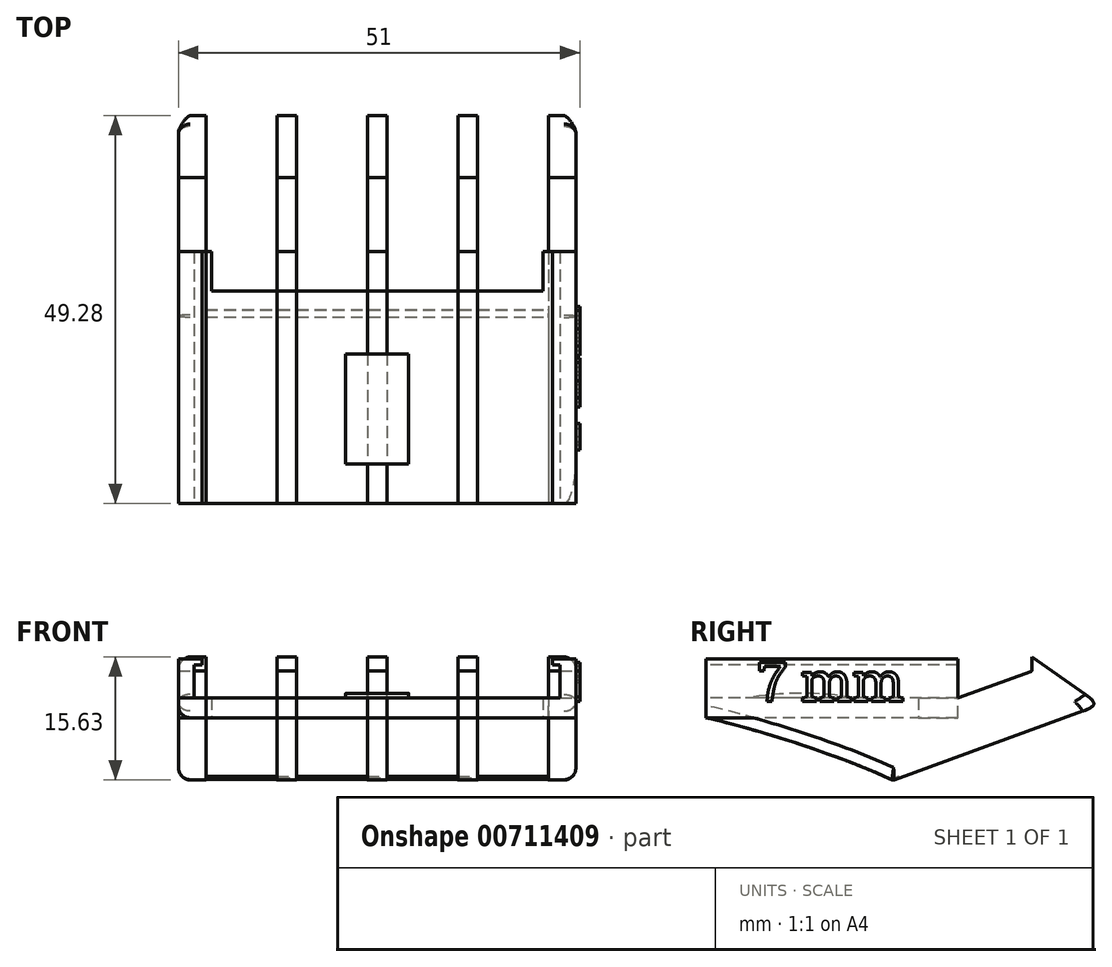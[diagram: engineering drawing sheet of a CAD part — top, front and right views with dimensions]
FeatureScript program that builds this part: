
annotation { "Feature Type Name" : "Feature", "Feature Type Description" : "" }
export const myFeature = defineFeature(function(context is Context, id is Id, definition is map)
    precondition{}
    {
        {
            var Q0;
            Q0=qCreatedBy(makeId("Top.planeOp"),FACE);
            var sketch = newSketch(context, id + "F0", { "sketchPlane" : qUnion([Q0])});
            skLineSegment(sketch, "E0.top", {"start": v(25.25, -16) * mm, "end": v(-25.25, -16) * mm});
            skLineSegment(sketch, "E0.left", {"start": v(25.25, 16) * mm, "end": v(25.25, -16) * mm});
            skLineSegment(sketch, "E0.right", {"start": v(-25.25, 16) * mm, "end": v(-25.25, -16) * mm});
            skPoint(sketch, "E0.middle", {"position": v(0, 0) * mm});
            skLineSegment(sketch, "E1", {"start": v(-21.05, 11) * mm, "end": v(21.05, 11) * mm});
            skLineSegment(sketch, "E2", {"start": v(21.05, 11) * mm, "end": v(21.05, 16) * mm});
            skLineSegment(sketch, "E3", {"start": v(21.05, 16) * mm, "end": v(25.25, 16) * mm});
            skLineSegment(sketch, "E4", {"start": v(-21.05, 11) * mm, "end": v(-21.05, 16) * mm});
            skLineSegment(sketch, "E5", {"start": v(-21.05, 16) * mm, "end": v(-25.25, 16) * mm});
            skSolve(sketch);
        }
        {
            var Q0;
            Q0 = qSketchRegion(id + "F0", true);
            extrude(context, id + "F1", {"entities" : qUnion([Q0]), "depth" : 2.5 * mm, "offsetDistance" : 25 * mm});
        }
        {
            var Q0;
            Q0=makeQuery(id+"F1.opExtrude","SWEPT_FACE",FACE,{"disambiguationData":[OSD([sQuery(id+"F0.wireOp",EDGE,"E0.top")])]});
            var sketch = newSketch(context, id + "F2", { "sketchPlane" : qUnion([Q0])});
            skLineSegment(sketch, "E6.0", {"start": v(25.25, 2.5) * mm, "end": v(-25.25, 2.5) * mm});
            skLineSegment(sketch, "E7", {"start": v(25.25, 2.5) * mm, "end": v(25.25, 7.5) * mm});
            skLineSegment(sketch, "E8", {"start": v(25.25, 7.5) * mm, "end": v(22.25, 7.5) * mm});
            skLineSegment(sketch, "E9", {"start": v(22.25, 7.5) * mm, "end": v(22.25, 6.7) * mm});
            skLineSegment(sketch, "E10", {"start": v(22.25, 6.7) * mm, "end": v(23.25, 6.7) * mm});
            skLineSegment(sketch, "E11", {"start": v(23.25, 6.7) * mm, "end": v(23.25, 2.5) * mm});
            skLineSegment(sketch, "E12", {"start": v(23.25, 2.5) * mm, "end": v(25.25, 2.5) * mm});
            skLineSegment(sketch, "E13.MirrorCS", {"start": v(-25.25, 2.5) * mm, "end": v(-25.25, 7.5) * mm});
            skLineSegment(sketch, "E14.MirrorCS", {"start": v(-25.25, 7.5) * mm, "end": v(-22.25, 7.5) * mm});
            skLineSegment(sketch, "E15.MirrorCS", {"start": v(-22.25, 7.5) * mm, "end": v(-22.25, 6.7) * mm});
            skLineSegment(sketch, "E16.MirrorCS", {"start": v(-22.25, 6.7) * mm, "end": v(-23.25, 6.7) * mm});
            skLineSegment(sketch, "E17.MirrorCS", {"start": v(-23.25, 6.7) * mm, "end": v(-23.25, 2.5) * mm});
            skSolve(sketch);
        }
        {
            var Q0;
            Q0 = qSketchRegion(id + "F2", true);
            var Q1;
            Q1=makeQuery(id+"F1.opExtrude","SWEPT_FACE",FACE,{"disambiguationData":[OSD([sQuery(id+"F0.wireOp",EDGE,"E3")])]});
            extrude(context, id + "F3", {"entities" : qUnion([Q0]), "operationType" : NewBodyOperationType.ADD, "endBound" : BoundingType.UP_TO_SURFACE, "oppositeDirection" : true, "depth" : 25 * mm, "endBoundEntityFace" : qUnion([Q1]), "offsetDistance" : 25 * mm});
        }
        {
            var Q0;
            Q0=makeQuery(id+"F3.boolean.opBoolean","MERGE",FACE,{"derivedFrom":[makeQuery(id+"F1.opExtrude","SWEPT_FACE",FACE,{"disambiguationData":[OSD([sQuery(id+"F0.wireOp",EDGE,"E0.left")])]}),makeQuery(id+"F3.opExtrude","SWEPT_FACE",FACE,{"disambiguationData":[OSD([sQuery(id+"F2.wireOp",EDGE,"E7")])]})]});
            var sketch = newSketch(context, id + "F4", { "sketchPlane" : qUnion([Q0])});
            skLineSegment(sketch, "E18.0", {"start": v(16, 2.5) * mm, "end": v(-16, 2.5) * mm});
            skLineSegment(sketch, "E19.0", {"start": v(11, 2.5) * mm, "end": v(11, 0) * mm});
            skLineSegment(sketch, "E20.0", {"start": v(16, 0) * mm, "end": v(-16, 0) * mm});
            skLineSegment(sketch, "E21.0", {"start": v(16, 2.5) * mm, "end": v(16, 0) * mm});
            skLineSegment(sketch, "E22", {"start": v(11, 0) * mm, "end": v(11, 2.5) * mm});
            skLineSegment(sketch, "E23", {"start": v(11, 2.5) * mm, "end": v(16, 2.5) * mm});
            skLineSegment(sketch, "E24", {"start": v(16, 2.5) * mm, "end": v(25.4, 5.92) * mm});
            skLineSegment(sketch, "E25", {"start": v(25.4, 5.92) * mm, "end": v(25.4, 7.72) * mm});
            skLineSegment(sketch, "E26", {"start": v(25.4, 7.72) * mm, "end": v(34.09, 1.63) * mm});
            skLineSegment(sketch, "E27", {"start": v(34.09, 1.63) * mm, "end": v(7.78, -7.94) * mm});
            skFitSpline(sketch, "E28", {"points": [v(7.78, -7.94) * mm, v(-16, 0) * mm], "startDerivative": vector(-23.73, 11.08) * mm, "endDerivative": vector(-13.12, 2.78) * mm});
            skSolve(sketch);
        }
        {
            var Q0;
            Q0 = qSketchRegion(id + "F4", true);
            var Q1;
            Q1=makeQuery(id+"F3.boolean.opBoolean","MERGE",FACE,{"derivedFrom":[makeQuery(id+"F1.opExtrude","SWEPT_FACE",FACE,{"disambiguationData":[OSD([sQuery(id+"F0.wireOp",EDGE,"E0.right")])]}),makeQuery(id+"F3.opExtrude","SWEPT_FACE",FACE,{"disambiguationData":[OSD([sQuery(id+"F2.wireOp",EDGE,"E13.MirrorCS")])]})]});
            extrude(context, id + "F5", {"entities" : qUnion([Q0]), "operationType" : NewBodyOperationType.ADD, "endBound" : BoundingType.UP_TO_SURFACE, "oppositeDirection" : true, "depth" : 25 * mm, "endBoundEntityFace" : qUnion([Q1]), "offsetDistance" : 25 * mm});
        }
        {
            var Q0;
            Q0=makeQuery(id+"F5.opExtrude","SWEPT_FACE",FACE,{"disambiguationData":[OSD([sQuery(id+"F4.wireOp",EDGE,"E27")])]});
            var sketch = newSketch(context, id + "F6", { "sketchPlane" : qUnion([Q0])});
            skLineSegment(sketch, "E29.bottom", {"start": v(21.75, -32.6) * mm, "end": v(12.75, -32.6) * mm});
            skLineSegment(sketch, "E29.top", {"start": v(21.75, 31.14) * mm, "end": v(12.75, 31.14) * mm});
            skLineSegment(sketch, "E29.left", {"start": v(21.75, -32.6) * mm, "end": v(21.75, 31.14) * mm});
            skLineSegment(sketch, "E29.right", {"start": v(12.75, -32.6) * mm, "end": v(12.75, 31.14) * mm});
            skLineSegment(sketch, "E30.1.0.0", {"start": v(10.25, -32.6) * mm, "end": v(10.25, 31.14) * mm});
            skLineSegment(sketch, "E30.1.0.1", {"start": v(1.25, -32.6) * mm, "end": v(1.25, 31.14) * mm});
            skLineSegment(sketch, "E30.1.0.2", {"start": v(10.25, 31.14) * mm, "end": v(1.25, 31.14) * mm});
            skLineSegment(sketch, "E30.1.0.3", {"start": v(10.25, -32.6) * mm, "end": v(1.25, -32.6) * mm});
            skLineSegment(sketch, "E30.2.0.0", {"start": v(-1.25, -32.6) * mm, "end": v(-1.25, 31.14) * mm});
            skLineSegment(sketch, "E30.2.0.1", {"start": v(-10.25, -32.6) * mm, "end": v(-10.25, 31.14) * mm});
            skLineSegment(sketch, "E30.2.0.2", {"start": v(-1.25, 31.14) * mm, "end": v(-10.25, 31.14) * mm});
            skLineSegment(sketch, "E30.2.0.3", {"start": v(-1.25, -32.6) * mm, "end": v(-10.25, -32.6) * mm});
            skLineSegment(sketch, "E30.3.0.0", {"start": v(-12.75, -32.6) * mm, "end": v(-12.75, 31.14) * mm});
            skLineSegment(sketch, "E30.3.0.1", {"start": v(-21.75, -32.6) * mm, "end": v(-21.75, 31.14) * mm});
            skLineSegment(sketch, "E30.3.0.2", {"start": v(-12.75, 31.14) * mm, "end": v(-21.75, 31.14) * mm});
            skLineSegment(sketch, "E30.3.0.3", {"start": v(-12.75, -32.6) * mm, "end": v(-21.75, -32.6) * mm});
            skLineSegment(sketch, "E30.direction1", {"start": v(21.75, -32.6) * mm, "end": v(10.25, -32.6) * mm, "construction": true});
            skSolve(sketch);
        }
        {
            var Q0;
            Q0 = qSketchRegion(id + "F6", true);
            extrude(context, id + "F7", {"entities" : qUnion([Q0]), "operationType" : NewBodyOperationType.REMOVE, "endBound" : BoundingType.UP_TO_NEXT, "oppositeDirection" : true, "depth" : 25 * mm, "offsetDistance" : 25 * mm});
        }
        {
            var Q0;
            Q0 = qSketchRegion(id + "F0", true);
            extrude(context, id + "F8", {"entities" : qUnion([Q0]), "depth" : 2.5 * mm, "offsetDistance" : 25 * mm});
        }
        {
            var Q0;
            Q0=qCreatedBy(makeId("Right.planeOp"),FACE);
            var sketch = newSketch(context, id + "F9", { "sketchPlane" : qUnion([Q0])});
            skLineSegment(sketch, "E31.0", {"start": v(16, 2.5) * mm, "end": v(-16, 2.5) * mm});
            skLineSegment(sketch, "E32.0", {"start": v(11, 2.5) * mm, "end": v(11, 0) * mm});
            skArc(sketch, "E33", {"start": v(3, 2.5) * mm, "mid": v(-4, 3.1) * mm, "end": v(-11, 2.5) * mm});
            skSolve(sketch);
        }
        {
            var Q0;
            Q0 = qSketchRegion(id + "F9", true);
            extrude(context, id + "F10", {"entities" : qUnion([Q0]), "endBound" : BoundingType.SYMMETRIC, "depth" : 8 * mm, "offsetDistance" : 25 * mm});
        }
        {
            var Q0;
            {var subQ0=sQuery(id+"F4.wireOp",EDGE,"E26");var subQ1=sQuery(id+"F4.wireOp",EDGE,"E27");Q0=makeQuery(id+"F7.boolean.opBoolean","SPLIT",EDGE,{"disambiguationData":[TD([makeQuery(id+"F1.opExtrude","SWEPT_FACE",FACE,{"disambiguationData":[OSD([sQuery(id+"F0.wireOp",EDGE,"E0.right")])]})])],"derivedFrom":makeQuery(id+"F5.opExtrude","SWEPT_EDGE",EDGE,{"disambiguationData":[OSD([subQ0,subQ1])]})});}
            var Q1;
            {var subQ0=sQuery(id+"F4.wireOp",EDGE,"E26");var subQ1=sQuery(id+"F4.wireOp",EDGE,"E27");Q1=makeQuery(id+"F7.boolean.opBoolean","SPLIT",EDGE,{"disambiguationData":[TD([makeQuery(id+"F7.opExtrude","SWEPT_FACE",FACE,{"disambiguationData":[OSD([sQuery(id+"F6.wireOp",EDGE,"E30.8.0.1")])]})])],"derivedFrom":makeQuery(id+"F5.opExtrude","SWEPT_EDGE",EDGE,{"disambiguationData":[OSD([subQ0,subQ1])]})});}
            var Q2;
            {var subQ0=sQuery(id+"F4.wireOp",EDGE,"E26");var subQ1=sQuery(id+"F4.wireOp",EDGE,"E27");Q2=makeQuery(id+"F7.boolean.opBoolean","SPLIT",EDGE,{"disambiguationData":[TD([makeQuery(id+"F7.opExtrude","SWEPT_FACE",FACE,{"disambiguationData":[OSD([sQuery(id+"F6.wireOp",EDGE,"E30.7.0.1")])]})])],"derivedFrom":makeQuery(id+"F5.opExtrude","SWEPT_EDGE",EDGE,{"disambiguationData":[OSD([subQ0,subQ1])]})});}
            var Q3;
            {var subQ0=sQuery(id+"F4.wireOp",EDGE,"E26");var subQ1=sQuery(id+"F4.wireOp",EDGE,"E27");Q3=makeQuery(id+"F7.boolean.opBoolean","SPLIT",EDGE,{"disambiguationData":[TD([makeQuery(id+"F7.opExtrude","SWEPT_FACE",FACE,{"disambiguationData":[OSD([sQuery(id+"F6.wireOp",EDGE,"E30.6.0.1")])]})])],"derivedFrom":makeQuery(id+"F5.opExtrude","SWEPT_EDGE",EDGE,{"disambiguationData":[OSD([subQ0,subQ1])]})});}
            var Q4;
            {var subQ0=sQuery(id+"F4.wireOp",EDGE,"E26");var subQ1=sQuery(id+"F4.wireOp",EDGE,"E27");Q4=makeQuery(id+"F7.boolean.opBoolean","SPLIT",EDGE,{"disambiguationData":[TD([makeQuery(id+"F7.opExtrude","SWEPT_FACE",FACE,{"disambiguationData":[OSD([sQuery(id+"F6.wireOp",EDGE,"E30.5.0.1")])]})])],"derivedFrom":makeQuery(id+"F5.opExtrude","SWEPT_EDGE",EDGE,{"disambiguationData":[OSD([subQ0,subQ1])]})});}
            var Q5;
            {var subQ0=sQuery(id+"F4.wireOp",EDGE,"E26");var subQ1=sQuery(id+"F4.wireOp",EDGE,"E27");Q5=makeQuery(id+"F7.boolean.opBoolean","SPLIT",EDGE,{"disambiguationData":[TD([makeQuery(id+"F7.opExtrude","SWEPT_FACE",FACE,{"disambiguationData":[OSD([sQuery(id+"F6.wireOp",EDGE,"E30.4.0.1")])]})])],"derivedFrom":makeQuery(id+"F5.opExtrude","SWEPT_EDGE",EDGE,{"disambiguationData":[OSD([subQ0,subQ1])]})});}
            var Q6;
            {var subQ0=sQuery(id+"F4.wireOp",EDGE,"E26");var subQ1=sQuery(id+"F4.wireOp",EDGE,"E27");Q6=makeQuery(id+"F7.boolean.opBoolean","SPLIT",EDGE,{"disambiguationData":[TD([makeQuery(id+"F7.opExtrude","SWEPT_FACE",FACE,{"disambiguationData":[OSD([sQuery(id+"F6.wireOp",EDGE,"E30.3.0.1")])]})])],"derivedFrom":makeQuery(id+"F5.opExtrude","SWEPT_EDGE",EDGE,{"disambiguationData":[OSD([subQ0,subQ1])]})});}
            var Q7;
            {var subQ0=sQuery(id+"F4.wireOp",EDGE,"E26");var subQ1=sQuery(id+"F4.wireOp",EDGE,"E27");Q7=makeQuery(id+"F7.boolean.opBoolean","SPLIT",EDGE,{"disambiguationData":[TD([makeQuery(id+"F7.opExtrude","SWEPT_FACE",FACE,{"disambiguationData":[OSD([sQuery(id+"F6.wireOp",EDGE,"E30.2.0.1")])]})])],"derivedFrom":makeQuery(id+"F5.opExtrude","SWEPT_EDGE",EDGE,{"disambiguationData":[OSD([subQ0,subQ1])]})});}
            var Q8;
            {var subQ0=sQuery(id+"F4.wireOp",EDGE,"E26");var subQ1=sQuery(id+"F4.wireOp",EDGE,"E27");Q8=makeQuery(id+"F7.boolean.opBoolean","SPLIT",EDGE,{"disambiguationData":[TD([makeQuery(id+"F7.opExtrude","SWEPT_FACE",FACE,{"disambiguationData":[OSD([sQuery(id+"F6.wireOp",EDGE,"E30.1.0.1")])]})])],"derivedFrom":makeQuery(id+"F5.opExtrude","SWEPT_EDGE",EDGE,{"disambiguationData":[OSD([subQ0,subQ1])]})});}
            var Q9;
            {var subQ0=sQuery(id+"F4.wireOp",EDGE,"E26");var subQ1=sQuery(id+"F4.wireOp",EDGE,"E27");Q9=makeQuery(id+"F7.boolean.opBoolean","SPLIT",EDGE,{"disambiguationData":[TD([makeQuery(id+"F7.opExtrude","SWEPT_FACE",FACE,{"disambiguationData":[OSD([sQuery(id+"F6.wireOp",EDGE,"E29.right")])]})])],"derivedFrom":makeQuery(id+"F5.opExtrude","SWEPT_EDGE",EDGE,{"disambiguationData":[OSD([subQ0,subQ1])]})});}
            var Q10;
            {var subQ0=sQuery(id+"F4.wireOp",EDGE,"E26");var subQ1=sQuery(id+"F4.wireOp",EDGE,"E27");Q10=makeQuery(id+"F7.boolean.opBoolean","SPLIT",EDGE,{"disambiguationData":[TD([makeQuery(id+"F1.opExtrude","SWEPT_FACE",FACE,{"disambiguationData":[OSD([sQuery(id+"F0.wireOp",EDGE,"E0.left")])]})])],"derivedFrom":makeQuery(id+"F5.opExtrude","SWEPT_EDGE",EDGE,{"disambiguationData":[OSD([subQ0,subQ1])]})});}
            fillet(context, id + "F11", {"entities" : qUnion([Q0, Q1, Q2, Q3, Q4, Q5, Q6, Q7, Q8, Q9, Q10]), "radius" : 1.2 * mm, "tangentPropagation" : true, "rho" : 0.6, "crossSection" : FilletCrossSection.CONIC, "allowEdgeOverflow" : false});
        }
        {
            var Q0;
            {var subQ2=sQuery(id+"F4.wireOp",EDGE,"E27");Q0=makeQuery(id+"F7.boolean.opBoolean","SPLIT",FACE,{"disambiguationData":[TD([makeQuery(id+"F1.opExtrude","SWEPT_FACE",FACE,{"disambiguationData":[OSD([sQuery(id+"F0.wireOp",EDGE,"E0.right")])]})])],"derivedFrom":makeQuery(id+"F5.opExtrude","SWEPT_FACE",FACE,{"disambiguationData":[OSD([subQ2])]})});}
            var sketch = newSketch(context, id + "F12", { "sketchPlane" : qUnion([Q0])});
            skLineSegment(sketch, "E34.bottom", {"start": v(-25.25, -4.6) * mm, "end": v(21.75, -4.6) * mm});
            skLineSegment(sketch, "E34.top", {"start": v(-21.75, -5.5) * mm, "end": v(21.75, -5.5) * mm});
            skLineSegment(sketch, "E35.0", {"start": v(21.75, -30.29) * mm, "end": v(21.75, -4.6) * mm});
            skLineSegment(sketch, "E36", {"start": v(21.75, -5.5) * mm, "end": v(21.75, -4.6) * mm});
            skLineSegment(sketch, "E37.0", {"start": v(-21.75, -30.29) * mm, "end": v(-21.75, -4.6) * mm});
            skLineSegment(sketch, "E38", {"start": v(-21.75, -5.5) * mm, "end": v(-21.75, -4.6) * mm});
            skSolve(sketch);
        }
        {
            var Q0;
            Q0 = qSketchRegion(id + "F12", true);
            extrude(context, id + "F13", {"entities" : qUnion([Q0]), "oppositeDirection" : true, "depth" : 0.2 * mm, "offsetDistance" : 25 * mm});
        }
        {
            var Q0;
            {var subQ0=sQuery(id+"F4.wireOp",EDGE,"E27");var subQ1=sQuery(id+"F4.wireOp",EDGE,"E28");Q0=makeQuery(id+"F7.boolean.opBoolean","SPLIT",EDGE,{"disambiguationData":[TD([makeQuery(id+"F1.opExtrude","SWEPT_FACE",FACE,{"disambiguationData":[OSD([sQuery(id+"F0.wireOp",EDGE,"E0.left")])]})])],"derivedFrom":makeQuery(id+"F5.opExtrude","SWEPT_EDGE",EDGE,{"disambiguationData":[OSD([subQ0,subQ1])]})});}
            var Q1;
            {var subQ0=sQuery(id+"F4.wireOp",EDGE,"E27");var subQ1=sQuery(id+"F4.wireOp",EDGE,"E28");Q1=makeQuery(id+"F7.boolean.opBoolean","SPLIT",EDGE,{"disambiguationData":[TD([makeQuery(id+"F7.opExtrude","SWEPT_FACE",FACE,{"disambiguationData":[OSD([sQuery(id+"F6.wireOp",EDGE,"E29.right")])]})])],"derivedFrom":makeQuery(id+"F5.opExtrude","SWEPT_EDGE",EDGE,{"disambiguationData":[OSD([subQ0,subQ1])]})});}
            var Q2;
            {var subQ0=sQuery(id+"F4.wireOp",EDGE,"E27");var subQ1=sQuery(id+"F4.wireOp",EDGE,"E28");Q2=makeQuery(id+"F7.boolean.opBoolean","SPLIT",EDGE,{"disambiguationData":[TD([makeQuery(id+"F7.opExtrude","SWEPT_FACE",FACE,{"disambiguationData":[OSD([sQuery(id+"F6.wireOp",EDGE,"E30.1.0.1")])]})])],"derivedFrom":makeQuery(id+"F5.opExtrude","SWEPT_EDGE",EDGE,{"disambiguationData":[OSD([subQ0,subQ1])]})});}
            var Q3;
            {var subQ0=sQuery(id+"F4.wireOp",EDGE,"E27");var subQ1=sQuery(id+"F4.wireOp",EDGE,"E28");Q3=makeQuery(id+"F7.boolean.opBoolean","SPLIT",EDGE,{"disambiguationData":[TD([makeQuery(id+"F7.opExtrude","SWEPT_FACE",FACE,{"disambiguationData":[OSD([sQuery(id+"F6.wireOp",EDGE,"E30.2.0.1")])]})])],"derivedFrom":makeQuery(id+"F5.opExtrude","SWEPT_EDGE",EDGE,{"disambiguationData":[OSD([subQ0,subQ1])]})});}
            var Q4;
            {var subQ0=sQuery(id+"F4.wireOp",EDGE,"E27");var subQ1=sQuery(id+"F4.wireOp",EDGE,"E28");Q4=makeQuery(id+"F7.boolean.opBoolean","SPLIT",EDGE,{"disambiguationData":[TD([makeQuery(id+"F7.opExtrude","SWEPT_FACE",FACE,{"disambiguationData":[OSD([sQuery(id+"F6.wireOp",EDGE,"E30.3.0.1")])]})])],"derivedFrom":makeQuery(id+"F5.opExtrude","SWEPT_EDGE",EDGE,{"disambiguationData":[OSD([subQ0,subQ1])]})});}
            var Q5;
            {var subQ0=sQuery(id+"F4.wireOp",EDGE,"E27");var subQ1=sQuery(id+"F4.wireOp",EDGE,"E28");Q5=makeQuery(id+"F7.boolean.opBoolean","SPLIT",EDGE,{"disambiguationData":[TD([makeQuery(id+"F7.opExtrude","SWEPT_FACE",FACE,{"disambiguationData":[OSD([sQuery(id+"F6.wireOp",EDGE,"E30.4.0.1")])]})])],"derivedFrom":makeQuery(id+"F5.opExtrude","SWEPT_EDGE",EDGE,{"disambiguationData":[OSD([subQ0,subQ1])]})});}
            var Q6;
            {var subQ0=sQuery(id+"F4.wireOp",EDGE,"E27");var subQ1=sQuery(id+"F4.wireOp",EDGE,"E28");Q6=makeQuery(id+"F7.boolean.opBoolean","SPLIT",EDGE,{"disambiguationData":[TD([makeQuery(id+"F7.opExtrude","SWEPT_FACE",FACE,{"disambiguationData":[OSD([sQuery(id+"F6.wireOp",EDGE,"E30.5.0.1")])]})])],"derivedFrom":makeQuery(id+"F5.opExtrude","SWEPT_EDGE",EDGE,{"disambiguationData":[OSD([subQ0,subQ1])]})});}
            var Q7;
            {var subQ0=sQuery(id+"F4.wireOp",EDGE,"E27");var subQ1=sQuery(id+"F4.wireOp",EDGE,"E28");Q7=makeQuery(id+"F7.boolean.opBoolean","SPLIT",EDGE,{"disambiguationData":[TD([makeQuery(id+"F7.opExtrude","SWEPT_FACE",FACE,{"disambiguationData":[OSD([sQuery(id+"F6.wireOp",EDGE,"E30.6.0.1")])]})])],"derivedFrom":makeQuery(id+"F5.opExtrude","SWEPT_EDGE",EDGE,{"disambiguationData":[OSD([subQ0,subQ1])]})});}
            var Q8;
            {var subQ0=sQuery(id+"F4.wireOp",EDGE,"E27");var subQ1=sQuery(id+"F4.wireOp",EDGE,"E28");Q8=makeQuery(id+"F7.boolean.opBoolean","SPLIT",EDGE,{"disambiguationData":[TD([makeQuery(id+"F7.opExtrude","SWEPT_FACE",FACE,{"disambiguationData":[OSD([sQuery(id+"F6.wireOp",EDGE,"E30.8.0.1")])]})])],"derivedFrom":makeQuery(id+"F5.opExtrude","SWEPT_EDGE",EDGE,{"disambiguationData":[OSD([subQ0,subQ1])]})});}
            var Q9;
            Q9=makeQuery(id+"F13.opExtrude","CAP_EDGE",EDGE,{"disambiguationData":[OSD([sQuery(id+"F12.wireOp",EDGE,"E34.bottom")])],"isStart":true});
            var Q10;
            {var subQ0=sQuery(id+"F4.wireOp",EDGE,"E27");var subQ1=sQuery(id+"F4.wireOp",EDGE,"E28");Q10=makeQuery(id+"F7.boolean.opBoolean","SPLIT",EDGE,{"disambiguationData":[TD([makeQuery(id+"F7.opExtrude","SWEPT_FACE",FACE,{"disambiguationData":[OSD([sQuery(id+"F6.wireOp",EDGE,"E30.7.0.1")])]})])],"derivedFrom":makeQuery(id+"F5.opExtrude","SWEPT_EDGE",EDGE,{"disambiguationData":[OSD([subQ0,subQ1])]})});}
            var Q11;
            {var subQ0=sQuery(id+"F4.wireOp",EDGE,"E27");var subQ1=sQuery(id+"F4.wireOp",EDGE,"E28");Q11=makeQuery(id+"F7.boolean.opBoolean","SPLIT",EDGE,{"disambiguationData":[TD([makeQuery(id+"F1.opExtrude","SWEPT_FACE",FACE,{"disambiguationData":[OSD([sQuery(id+"F0.wireOp",EDGE,"E0.right")])]})])],"derivedFrom":makeQuery(id+"F5.opExtrude","SWEPT_EDGE",EDGE,{"disambiguationData":[OSD([subQ0,subQ1])]})});}
            fillet(context, id + "F14", {"entities" : qUnion([Q0, Q1, Q2, Q3, Q4, Q5, Q6, Q7, Q8, Q9, Q10, Q11]), "radius" : 0.4 * mm, "tangentPropagation" : true, "allowEdgeOverflow" : false});
        }
        {
            var Q0;
            Q0=makeQuery(id+"F5.opExtrude","CAP_EDGE",EDGE,{"disambiguationData":[OSD([sQuery(id+"F4.wireOp",EDGE,"E27")])],"isStart":false});
            var Q1;
            Q1=makeQuery(id+"F5.opExtrude","CAP_EDGE",EDGE,{"disambiguationData":[OSD([sQuery(id+"F4.wireOp",EDGE,"E27")])],"isStart":true});
            fillet(context, id + "F15", {"entities" : qUnion([Q0, Q1]), "radius" : 1.5 * mm, "tangentPropagation" : true, "allowEdgeOverflow" : false});
        }
        {
            var Q0;
            Q0=makeQuery(id+"F5.boolean.opBoolean","MERGE",FACE,{"derivedFrom":[makeQuery(id+"F3.boolean.opBoolean","MERGE",FACE,{"derivedFrom":[makeQuery(id+"F1.opExtrude","SWEPT_FACE",FACE,{"disambiguationData":[OSD([sQuery(id+"F0.wireOp",EDGE,"E0.left")])]}),makeQuery(id+"F3.opExtrude","SWEPT_FACE",FACE,{"disambiguationData":[OSD([sQuery(id+"F2.wireOp",EDGE,"E7")])]})]}),makeQuery(id+"F5.opExtrude","CAP_FACE",FACE,{"disambiguationData":[OSD([sQuery(id+"F4.wireOp",EDGE,"E20.0"),sQuery(id+"F4.wireOp",EDGE,"E22"),sQuery(id+"F4.wireOp",EDGE,"E23"),sQuery(id+"F4.wireOp",EDGE,"E24"),sQuery(id+"F4.wireOp",EDGE,"E25"),sQuery(id+"F4.wireOp",EDGE,"E26"),sQuery(id+"F4.wireOp",EDGE,"E27"),sQuery(id+"F4.wireOp",EDGE,"E28")])],"isStart":true})]});
            var sketch = newSketch(context, id + "F16", { "sketchPlane" : qUnion([Q0])});
            skLineSegment(sketch, "E39.0", {"start": v(16, 0) * mm, "end": v(-16, 0) * mm});
            skText(sketch, "E40", { "text": "7 mm", "fontName": "RobotoSlab-Regular.ttf"});
            const initialGuessF16  = {"E40": [-0.00946, 0.0021, 1, 0, 0.005]};
            skSetInitialGuess(sketch, initialGuessF16);
            skSolve(sketch);
        }
        {
            var Q0;
            Q0 = qSketchRegion(id + "F16", true);
            var Q1;
            Q1 = qConstructionFilter(qBodyType(qCreatedBy(id + "F16" ,EDGE), BodyType.WIRE), ConstructionObject.NO);
            extrude(context, id + "F17", {"entities" : qUnion([Q0]), "operationType" : NewBodyOperationType.ADD, "surfaceEntities" : qUnion([Q1]), "depth" : 0.5 * mm, "offsetDistance" : 25 * mm});
        }
    });
